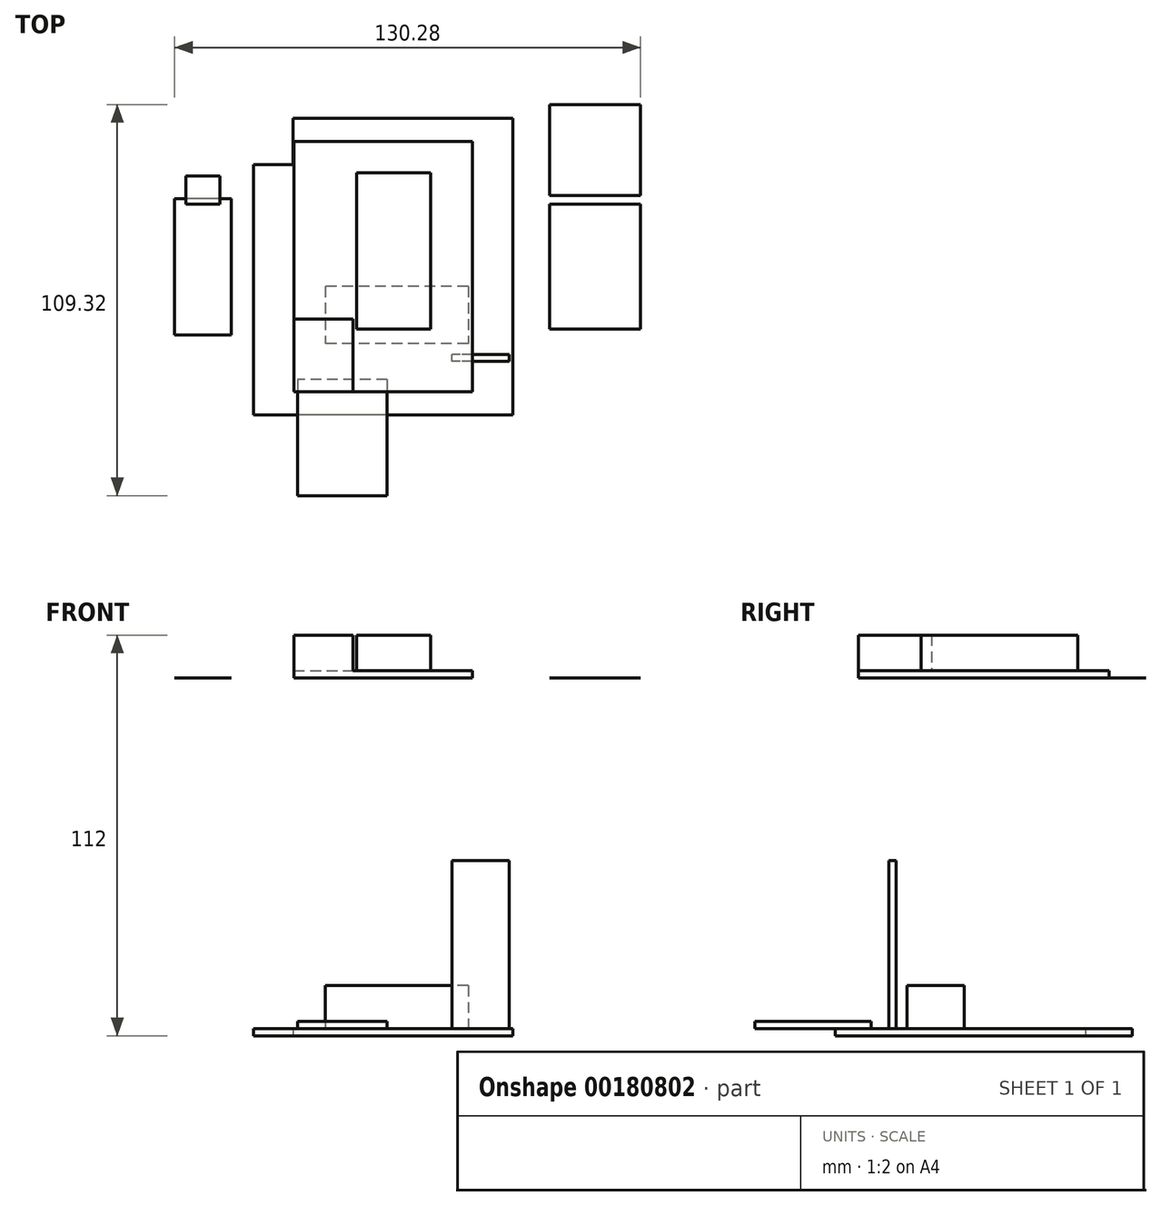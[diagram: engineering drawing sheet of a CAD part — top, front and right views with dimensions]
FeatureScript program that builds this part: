
annotation { "Feature Type Name" : "Feature", "Feature Type Description" : "" }
export const myFeature = defineFeature(function(context is Context, id is Id, definition is map)
    precondition{}
    {
        {
            var Q0;
            Q0=qCreatedBy(makeId("Top.planeOp"),FACE);
            var sketch = newSketch(context, id + "F0", { "sketchPlane" : qUnion([Q0])});
            skLineSegment(sketch, "E0.bottom", {"start": v(36.25, 41.5) * mm, "end": v(-36.25, 41.5) * mm});
            skLineSegment(sketch, "E0.top", {"start": v(36.25, -41.5) * mm, "end": v(-36.25, -41.5) * mm});
            skLineSegment(sketch, "E0.left", {"start": v(36.25, 41.5) * mm, "end": v(36.25, -41.5) * mm});
            skLineSegment(sketch, "E0.right", {"start": v(-36.25, 41.5) * mm, "end": v(-36.25, -41.5) * mm});
            skPoint(sketch, "E0.middle", {"position": v(0, 0) * mm});
            skLineSegment(sketch, "E1", {"start": v(-36.25, 28.5) * mm, "end": v(-25.25, 28.5) * mm});
            skLineSegment(sketch, "E2", {"start": v(-25.25, 28.5) * mm, "end": v(-25.25, 41.5) * mm});
            skSolve(sketch);
        }
        {
            var Q0;
            {var subQ1=sQuery(id+"F0.wireOp",EDGE,"E0.top");Q0=makeQuery(id+"F0.imprint","IMPRINT",FACE,{"disambiguationData":[TD([[makeQuery(id+"F0.imprint","IMPRINT",EDGE,{"derivedFrom":subQ1}),-1.0]])]});}
            extrude(context, id + "F1", {"entities" : qUnion([Q0]), "depth" : 2 * mm, "offsetDistance" : 25 * mm});
        }
        {
            var Q0;
            Q0=makeQuery(id+"F1.opExtrude","CAP_FACE",FACE,{"disambiguationData":[OSD([sQuery(id+"F0.wireOp",EDGE,"E0.bottom"),sQuery(id+"F0.wireOp",EDGE,"E0.top"),sQuery(id+"F0.wireOp",EDGE,"E0.left"),sQuery(id+"F0.wireOp",EDGE,"E0.right")])],"isStart":false});
            var sketch = newSketch(context, id + "F2", { "sketchPlane" : qUnion([Q0])});
            skLineSegment(sketch, "E3.bottom", {"start": v(1.09, -31.5) * mm, "end": v(-23.91, -31.5) * mm});
            skLineSegment(sketch, "E3.top", {"start": v(1.09, -64) * mm, "end": v(-23.91, -64) * mm});
            skLineSegment(sketch, "E3.left", {"start": v(1.09, -31.5) * mm, "end": v(1.09, -64) * mm});
            skLineSegment(sketch, "E3.right", {"start": v(-23.91, -31.5) * mm, "end": v(-23.91, -64) * mm});
            skPoint(sketch, "E3.middle", {"position": v(-11.41, -47.75) * mm});
            skSolve(sketch);
        }
        {
            var Q0;
            Q0 = qSketchRegion(id + "F2", true);
            extrude(context, id + "F3", {"entities" : qUnion([Q0]), "operationType" : NewBodyOperationType.ADD, "depth" : 2 * mm, "offsetDistance" : 25 * mm});
        }
        {
            var Q0;
            Q0=makeQuery(id+"F1.opExtrude","CAP_FACE",FACE,{"disambiguationData":[OSD([sQuery(id+"F0.wireOp",EDGE,"E0.bottom"),sQuery(id+"F0.wireOp",EDGE,"E0.top"),sQuery(id+"F0.wireOp",EDGE,"E0.left"),sQuery(id+"F0.wireOp",EDGE,"E0.right"),sQuery(id+"F0.wireOp",EDGE,"E1"),sQuery(id+"F0.wireOp",EDGE,"E2")])],"isStart":false});
            var sketch = newSketch(context, id + "F4", { "sketchPlane" : qUnion([Q0])});
            skLineSegment(sketch, "E4.bottom", {"start": v(35.25, -26.5) * mm, "end": v(19.25, -26.5) * mm});
            skLineSegment(sketch, "E4.top", {"start": v(35.25, -24.5) * mm, "end": v(19.25, -24.5) * mm});
            skLineSegment(sketch, "E4.left", {"start": v(35.25, -26.5) * mm, "end": v(35.25, -24.5) * mm});
            skLineSegment(sketch, "E4.right", {"start": v(19.25, -26.5) * mm, "end": v(19.25, -24.5) * mm});
            skPoint(sketch, "E4.middle", {"position": v(27.25, -25.5) * mm});
            skSolve(sketch);
        }
        {
            var Q0;
            Q0 = qSketchRegion(id + "F4", true);
            extrude(context, id + "F5", {"entities" : qUnion([Q0]), "operationType" : NewBodyOperationType.ADD, "depth" : 47 * mm, "offsetDistance" : 25 * mm});
        }
        {
            var Q0;
            Q0=makeQuery(id+"F1.opExtrude","CAP_FACE",FACE,{"disambiguationData":[OSD([sQuery(id+"F0.wireOp",EDGE,"E0.bottom"),sQuery(id+"F0.wireOp",EDGE,"E0.top"),sQuery(id+"F0.wireOp",EDGE,"E0.left"),sQuery(id+"F0.wireOp",EDGE,"E0.right"),sQuery(id+"F0.wireOp",EDGE,"E1"),sQuery(id+"F0.wireOp",EDGE,"E2")])],"isStart":false});
            var sketch = newSketch(context, id + "F6", { "sketchPlane" : qUnion([Q0])});
            skLineSegment(sketch, "E5.bottom", {"start": v(23.75, -5.5) * mm, "end": v(-16.25, -5.5) * mm});
            skLineSegment(sketch, "E5.top", {"start": v(23.75, -21.5) * mm, "end": v(-16.25, -21.5) * mm});
            skLineSegment(sketch, "E5.left", {"start": v(23.75, -5.5) * mm, "end": v(23.75, -21.5) * mm});
            skLineSegment(sketch, "E5.right", {"start": v(-16.25, -5.5) * mm, "end": v(-16.25, -21.5) * mm});
            skPoint(sketch, "E5.middle", {"position": v(3.75, -13.5) * mm});
            skSolve(sketch);
        }
        {
            var Q0;
            Q0=makeQuery(id+"F6.imprint","IMPRINT",FACE,{"disambiguationData":[TD([[makeQuery(id+"F6.imprint","IMPRINT",EDGE,{"derivedFrom":sQuery(id+"F6.wireOp",EDGE,"E5.bottom")}),1.0]])]});
            extrude(context, id + "F7", {"entities" : qUnion([Q0]), "operationType" : NewBodyOperationType.ADD, "depth" : 12 * mm, "offsetDistance" : 25 * mm});
        }
        {
            var Q0;
            Q0=qCreatedBy(makeId("Top.planeOp"),FACE);
            cPlane(context, id + "F8", {"entities" : qUnion([Q0]), "cplaneType" : CPlaneType.OFFSET, "offset" : 100 * mm, "width" : 150 * mm, "height" : 150 * mm});
        }
        {
            var Q0;
            Q0=qCreatedBy(id+"F8.planeOp",FACE);
            var sketch = newSketch(context, id + "F9", { "sketchPlane" : qUnion([Q0])});
            skLineSegment(sketch, "E6.bottom", {"start": v(25, 35) * mm, "end": v(-25, 35) * mm});
            skLineSegment(sketch, "E6.top", {"start": v(25, -35) * mm, "end": v(-25, -35) * mm});
            skLineSegment(sketch, "E6.left", {"start": v(25, 35) * mm, "end": v(25, -35) * mm});
            skLineSegment(sketch, "E6.right", {"start": v(-25, 35) * mm, "end": v(-25, -35) * mm});
            skPoint(sketch, "E6.middle", {"position": v(0, 0) * mm});
            skSolve(sketch);
        }
        {
            var Q0;
            Q0=makeQuery(id+"F9.imprint","IMPRINT",FACE,{"disambiguationData":[TD([[makeQuery(id+"F9.imprint","IMPRINT",EDGE,{"derivedFrom":sQuery(id+"F9.wireOp",EDGE,"E6.bottom")}),1.0]])]});
            extrude(context, id + "F10", {"entities" : qUnion([Q0]), "depth" : 2 * mm, "offsetDistance" : 25 * mm});
        }
        {
            var Q0;
            Q0=qCreatedBy(id+"F8.planeOp",FACE);
            var sketch = newSketch(context, id + "F11", { "sketchPlane" : qUnion([Q0])});
            skLineSegment(sketch, "E7.bottom", {"start": v(-42.48, 19.05) * mm, "end": v(-58.35, 19.05) * mm});
            skLineSegment(sketch, "E7.top", {"start": v(-42.48, -19.05) * mm, "end": v(-58.35, -19.05) * mm});
            skLineSegment(sketch, "E7.left", {"start": v(-42.48, 19.05) * mm, "end": v(-42.48, -19.05) * mm});
            skLineSegment(sketch, "E7.right", {"start": v(-58.35, 19.05) * mm, "end": v(-58.35, -19.05) * mm});
            skPoint(sketch, "E7.middle", {"position": v(-50.41, 0) * mm});
            skSolve(sketch);
        }
        {
            var Q0;
            Q0=makeQuery(id+"F11.imprint","IMPRINT",FACE,{"disambiguationData":[TD([[makeQuery(id+"F11.imprint","IMPRINT",EDGE,{"derivedFrom":sQuery(id+"F11.wireOp",EDGE,"E7.bottom")}),1.0]])]});
            extrude(context, id + "F12", {"entities" : qUnion([Q0]), "depth" : 3 / 406.4 * mm, "offsetDistance" : 25 * mm});
        }
        {
            var Q0;
            Q0=makeQuery(id+"F12.opExtrude","CAP_FACE",FACE,{"disambiguationData":[OSD([sQuery(id+"F11.wireOp",EDGE,"E7.bottom"),sQuery(id+"F11.wireOp",EDGE,"E7.top"),sQuery(id+"F11.wireOp",EDGE,"E7.left"),sQuery(id+"F11.wireOp",EDGE,"E7.right")])],"isStart":false});
            var sketch = newSketch(context, id + "F13", { "sketchPlane" : qUnion([Q0])});
            skLineSegment(sketch, "E8", {"start": v(-45.65, 17.46) * mm, "end": v(-45.65, 25.4) * mm});
            skLineSegment(sketch, "E9", {"start": v(-45.65, 25.4) * mm, "end": v(-55.18, 25.4) * mm});
            skLineSegment(sketch, "E10", {"start": v(-55.18, 25.4) * mm, "end": v(-55.18, 17.46) * mm});
            skLineSegment(sketch, "E11", {"start": v(-55.18, 17.46) * mm, "end": v(-45.65, 17.46) * mm});
            skSolve(sketch);
        }
        {
            var Q0;
            Q0 = qSketchRegion(id + "F13", true);
            extrude(context, id + "F14", {"entities" : qUnion([Q0]), "operationType" : NewBodyOperationType.ADD, "depth" : 1 / 406.4 * mm, "offsetDistance" : 25 * mm});
        }
        {
            var Q0;
            Q0=qCreatedBy(id+"F8.planeOp",FACE);
            var sketch = newSketch(context, id + "F15", { "sketchPlane" : qUnion([Q0])});
            skLineSegment(sketch, "E12.bottom", {"start": v(71.93, 17.46) * mm, "end": v(46.53, 17.46) * mm});
            skLineSegment(sketch, "E12.top", {"start": v(71.93, -17.46) * mm, "end": v(46.53, -17.46) * mm});
            skLineSegment(sketch, "E12.left", {"start": v(71.93, 17.46) * mm, "end": v(71.93, -17.46) * mm});
            skLineSegment(sketch, "E12.right", {"start": v(46.53, 17.46) * mm, "end": v(46.53, -17.46) * mm});
            skPoint(sketch, "E12.middle", {"position": v(59.23, 0) * mm});
            skSolve(sketch);
        }
        {
            var Q0;
            Q0 = qSketchRegion(id + "F15", true);
            extrude(context, id + "F16", {"entities" : qUnion([Q0]), "depth" : 2 / 406.4 * mm, "offsetDistance" : 25 * mm});
        }
        {
            var Q0;
            Q0=qCreatedBy(id+"F8.planeOp",FACE);
            var sketch = newSketch(context, id + "F17", { "sketchPlane" : qUnion([Q0])});
            skLineSegment(sketch, "E13.bottom", {"start": v(71.93, 45.32) * mm, "end": v(46.53, 45.32) * mm});
            skLineSegment(sketch, "E13.top", {"start": v(71.93, 19.92) * mm, "end": v(46.53, 19.92) * mm});
            skLineSegment(sketch, "E13.left", {"start": v(71.93, 45.32) * mm, "end": v(71.93, 19.92) * mm});
            skLineSegment(sketch, "E13.right", {"start": v(46.53, 45.32) * mm, "end": v(46.53, 19.92) * mm});
            skPoint(sketch, "E13.middle", {"position": v(59.23, 32.62) * mm});
            skLineSegment(sketch, "E14.0", {"start": v(71.93, 17.46) * mm, "end": v(46.53, 17.46) * mm, "construction": true});
            skLineSegment(sketch, "E15", {"start": v(59.23, 17.46) * mm, "end": v(59.23, 19.92) * mm, "construction": true});
            skSolve(sketch);
        }
        {
            var Q0;
            Q0=makeQuery(id+"F17.imprint","IMPRINT",FACE,{"disambiguationData":[TD([[makeQuery(id+"F17.imprint","IMPRINT",EDGE,{"derivedFrom":sQuery(id+"F17.wireOp",EDGE,"E13.bottom")}),1.0]])]});
            extrude(context, id + "F18", {"entities" : qUnion([Q0]), "depth" : 5 / 406.4 * mm, "offsetDistance" : 25 * mm});
        }
        {
            var Q0;
            Q0=makeQuery(id+"F10.opExtrude","CAP_FACE",FACE,{"disambiguationData":[OSD([sQuery(id+"F9.wireOp",EDGE,"E6.bottom"),sQuery(id+"F9.wireOp",EDGE,"E6.top"),sQuery(id+"F9.wireOp",EDGE,"E6.left"),sQuery(id+"F9.wireOp",EDGE,"E6.right")])],"isStart":false});
            var sketch = newSketch(context, id + "F19", { "sketchPlane" : qUnion([Q0])});
            skLineSegment(sketch, "E16.bottom", {"start": v(-7.4, 26.25) * mm, "end": v(13.2, 26.25) * mm});
            skLineSegment(sketch, "E16.top", {"start": v(-7.4, -17.5) * mm, "end": v(13.2, -17.5) * mm});
            skLineSegment(sketch, "E16.left", {"start": v(-7.4, 26.25) * mm, "end": v(-7.4, -17.5) * mm});
            skLineSegment(sketch, "E16.right", {"start": v(13.2, 26.25) * mm, "end": v(13.2, -17.5) * mm});
            skLineSegment(sketch, "E17.bottom", {"start": v(-25, -35) * mm, "end": v(-8.5, -35) * mm});
            skLineSegment(sketch, "E17.top", {"start": v(-25, -14.6) * mm, "end": v(-8.5, -14.6) * mm});
            skLineSegment(sketch, "E17.left", {"start": v(-25, -35) * mm, "end": v(-25, -14.6) * mm});
            skLineSegment(sketch, "E17.right", {"start": v(-8.5, -35) * mm, "end": v(-8.5, -14.6) * mm});
            skSolve(sketch);
        }
        {
            var Q0;
            Q0=makeQuery(id+"F19.imprint","IMPRINT",FACE,{"disambiguationData":[TD([[makeQuery(id+"F19.imprint","IMPRINT",EDGE,{"derivedFrom":sQuery(id+"F19.wireOp",EDGE,"E16.bottom")}),-1.0]])]});
            var Q1;
            Q1=makeQuery(id+"F19.imprint","IMPRINT",FACE,{"disambiguationData":[TD([[makeQuery(id+"F19.imprint","IMPRINT",EDGE,{"derivedFrom":sQuery(id+"F19.wireOp",EDGE,"E17.bottom")}),-1.0]])]});
            extrude(context, id + "F20", {"entities" : qUnion([Q0, Q1]), "operationType" : NewBodyOperationType.ADD, "depth" : 10 * mm, "offsetDistance" : 25 * mm});
        }
    });
